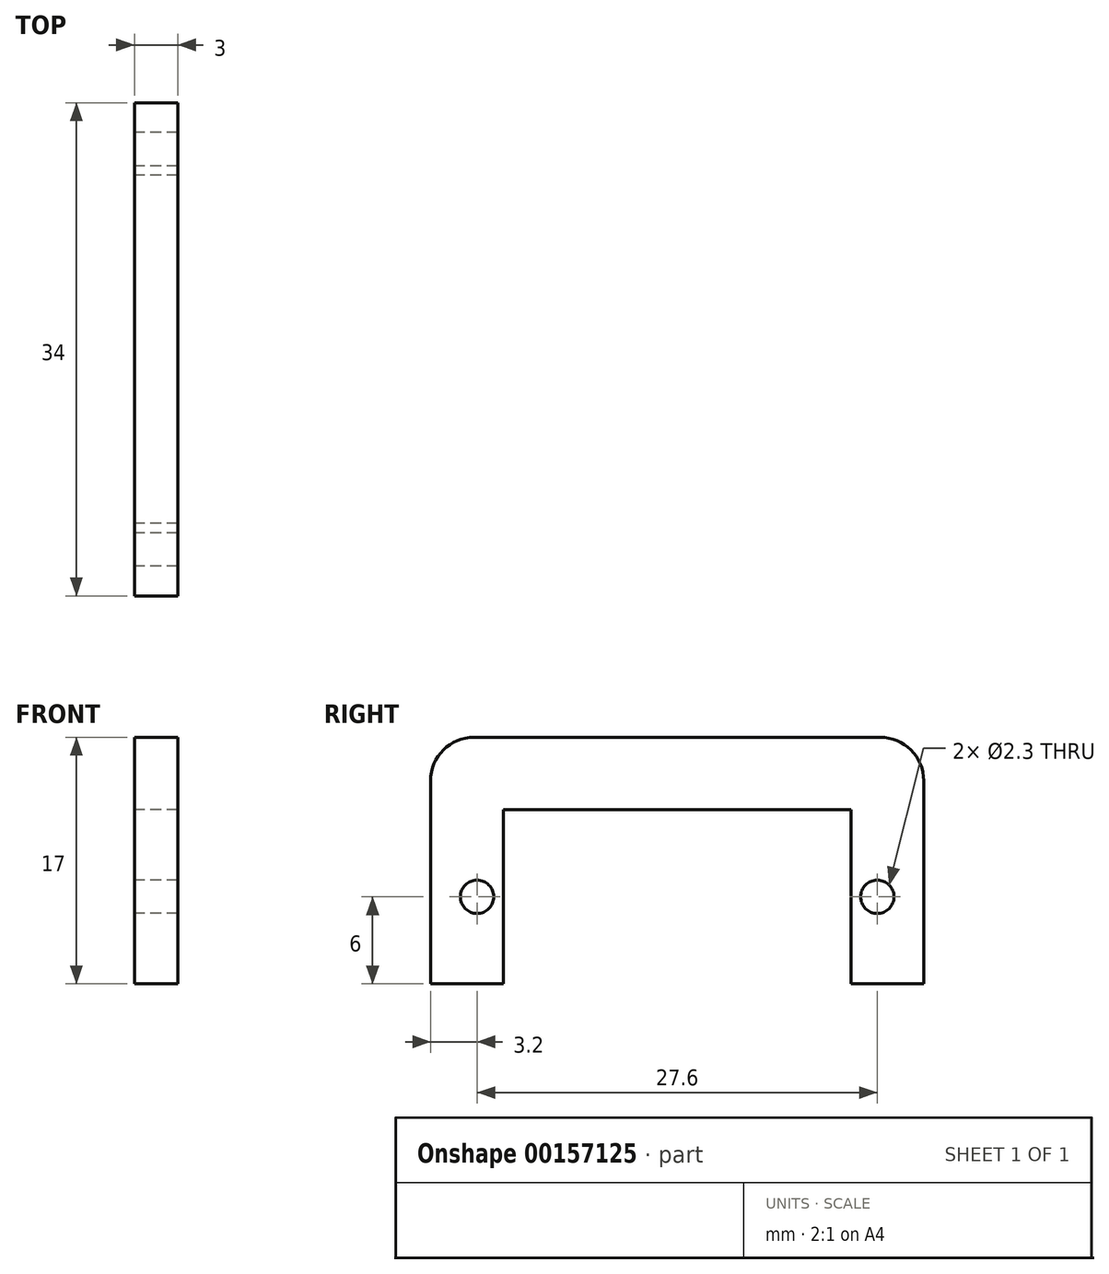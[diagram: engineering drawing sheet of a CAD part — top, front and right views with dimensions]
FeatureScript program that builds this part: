
annotation { "Feature Type Name" : "Feature", "Feature Type Description" : "" }
export const myFeature = defineFeature(function(context is Context, id is Id, definition is map)
    precondition{}
    {
        {
            var Q0;
            Q0=qCreatedBy(makeId("Right.planeOp"),FACE);
            var sketch = newSketch(context, id + "F0", { "sketchPlane" : qUnion([Q0])});
            skLineSegment(sketch, "E0.bottom", {"start": v(-12, 6) * mm, "end": v(12, 6) * mm});
            skLineSegment(sketch, "E0.top", {"start": v(-12, -6) * mm, "end": v(12, -6) * mm});
            skLineSegment(sketch, "E0.left", {"start": v(-12, 6) * mm, "end": v(-12, -6) * mm});
            skLineSegment(sketch, "E0.right", {"start": v(12, 6) * mm, "end": v(12, -6) * mm});
            skPoint(sketch, "E0.middle", {"position": v(0, 0) * mm});
            skLineSegment(sketch, "E1", {"start": v(-17, -6) * mm, "end": v(-17, 8) * mm});
            skLineSegment(sketch, "E2", {"start": v(-14, 11) * mm, "end": v(0, 11) * mm});
            skLineSegment(sketch, "E3", {"start": v(14, 11) * mm, "end": v(0, 11) * mm});
            skLineSegment(sketch, "E4", {"start": v(0, 6) * mm, "end": v(0, 11) * mm, "construction": true});
            skLineSegment(sketch, "E5", {"start": v(-17, 2.5) * mm, "end": v(-12, 2.5) * mm, "construction": true});
            skCircle(sketch, "E6", {"center": v(-13.8, 0) * mm, "radius": 1.15 * mm});
            skCircle(sketch, "E7", {"center": v(13.8, 0) * mm, "radius": 1.15 * mm});
            skLineSegment(sketch, "E8", {"start": v(-17, -6) * mm, "end": v(-12, -6) * mm});
            skLineSegment(sketch, "E9", {"start": v(17, -6) * mm, "end": v(12, -6) * mm});
            skPoint(sketch, "E10.visualSharp", {"position": v(-17, 11) * mm});
            skArc(sketch, "E10.filletArc", {"start": v(-14, 11) * mm, "mid": v(-16.12, 10.12) * mm, "end": v(-17, 8) * mm});
            skPoint(sketch, "E11.visualSharp", {"position": v(16.2, 11) * mm});
            skArc(sketch, "E11.filletArc", {"start": v(17, 8) * mm, "mid": v(16.12, 10.12) * mm, "end": v(14, 11) * mm});
            skLineSegment(sketch, "E12.trimOffspring", {"start": v(17, -6) * mm, "end": v(17, 8) * mm});
            skLineSegment(sketch, "E13", {"start": v(12, 3) * mm, "end": v(17, 3) * mm, "construction": true});
            skLineSegment(sketch, "E14", {"start": v(-12.65, 0) * mm, "end": v(-12, 0) * mm, "construction": true});
            skLineSegment(sketch, "E15", {"start": v(12.65, 0) * mm, "end": v(12, 0) * mm, "construction": true});
            skLineSegment(sketch, "E16", {"start": v(-13.8, 0) * mm, "end": v(13.8, 0) * mm});
            skSolve(sketch);
        }
        {
            var Q0;
            Q0=makeQuery(id+"F0.imprint","IMPRINT",FACE,{"disambiguationData":[TD([[makeQuery(id+"F0.imprint","IMPRINT",EDGE,{"derivedFrom":sQuery(id+"F0.wireOp",EDGE,"E0.bottom")}),1.0]])]});
            extrude(context, id + "F1", {"entities" : qUnion([Q0]), "depth" : 3 * mm});
        }
    });
